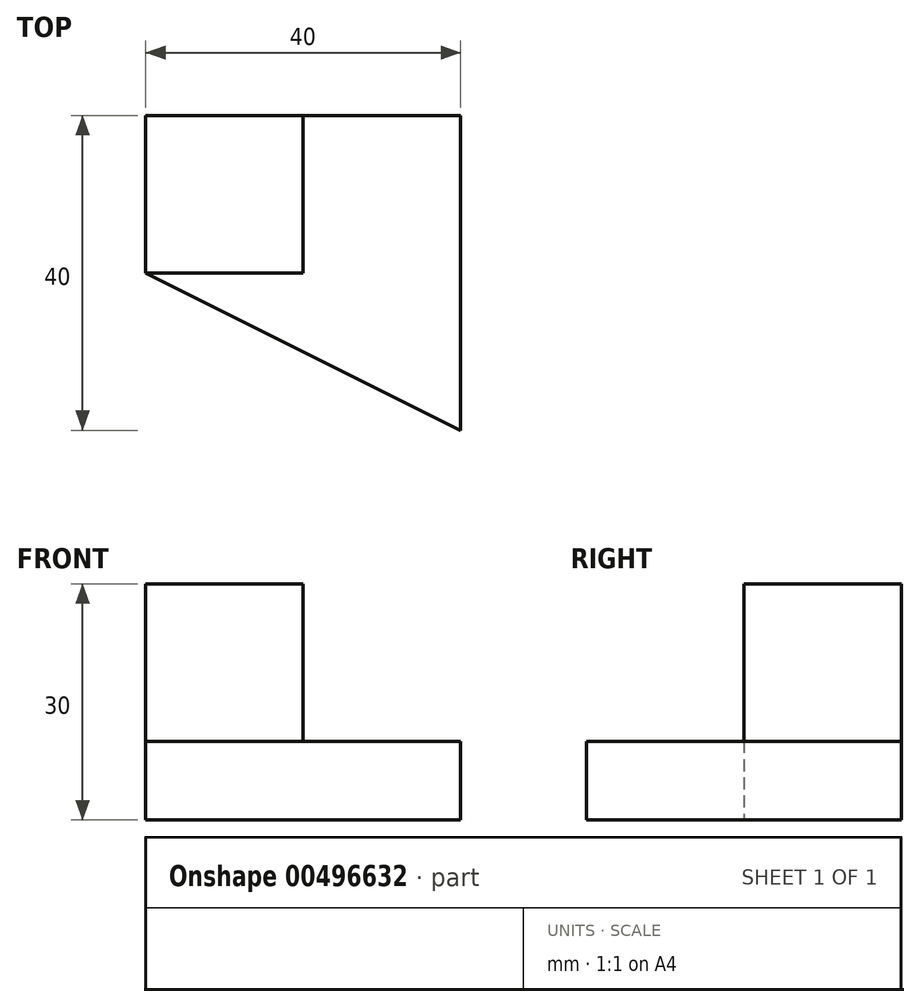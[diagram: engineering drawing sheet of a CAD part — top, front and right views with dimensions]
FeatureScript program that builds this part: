
annotation { "Feature Type Name" : "Feature", "Feature Type Description" : "" }
export const myFeature = defineFeature(function(context is Context, id is Id, definition is map)
    precondition{}
    {
        {
            var Q0;
            Q0=qCreatedBy(makeId("Top.planeOp"),FACE);
            var sketch = newSketch(context, id + "F0", { "sketchPlane" : qUnion([Q0])});
            skLineSegment(sketch, "E0", {"start": v(0, 0) * mm, "end": v(0, 20) * mm});
            skLineSegment(sketch, "E1", {"start": v(0, 20) * mm, "end": v(40, 20) * mm});
            skLineSegment(sketch, "E2", {"start": v(40, 20) * mm, "end": v(40, -20) * mm});
            skLineSegment(sketch, "E3", {"start": v(0, 0) * mm, "end": v(40, -20) * mm});
            skSolve(sketch);
        }
        {
            var Q0;
            Q0 = qSketchRegion(id + "F0", true);
            extrude(context, id + "F1", {"entities" : qUnion([Q0]), "depth" : 10 * mm});
        }
        {
            var Q0;
            Q0=makeQuery(id+"F1.opExtrude","CAP_FACE",FACE,{"disambiguationData":[OSD([sQuery(id+"F0.wireOp",EDGE,"E0"),sQuery(id+"F0.wireOp",EDGE,"E1"),sQuery(id+"F0.wireOp",EDGE,"E2"),sQuery(id+"F0.wireOp",EDGE,"E3")])],"isStart":false});
            var sketch = newSketch(context, id + "F2", { "sketchPlane" : qUnion([Q0])});
            skLineSegment(sketch, "E4.bottom", {"start": v(0, 20) * mm, "end": v(20, 20) * mm});
            skLineSegment(sketch, "E4.top", {"start": v(0, 0) * mm, "end": v(20, 0) * mm});
            skLineSegment(sketch, "E4.left", {"start": v(0, 20) * mm, "end": v(0, 0) * mm});
            skLineSegment(sketch, "E4.right", {"start": v(20, 20) * mm, "end": v(20, 0) * mm});
            skSolve(sketch);
        }
        {
            var Q0;
            Q0 = qSketchRegion(id + "F2", true);
            extrude(context, id + "F3", {"entities" : qUnion([Q0]), "operationType" : NewBodyOperationType.ADD, "depth" : 20 * mm});
        }
    });
